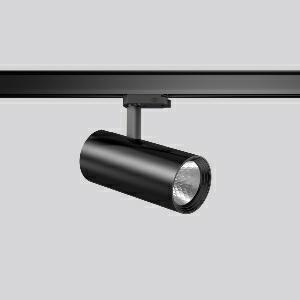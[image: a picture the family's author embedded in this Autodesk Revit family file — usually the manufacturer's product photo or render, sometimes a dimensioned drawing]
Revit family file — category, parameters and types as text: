
# Revit family: deecos_s_mini_742196_003_b451
name_source: partatom
category: Lighting Fixtures
units: mm (PartAtom-declared; Revit-internal decimal feet)

## family parameters
Cut with Voids When Loaded = No
Host = Face
Light Source = No
Part Type = Normal
Room Calculation Point = No
Round Connector Dimension = Use Diameter
Shared = No

## types (1)
- DEECOS S mini (1 x LED Modul 930, 2450 lm, 3000)
    Apparent Load = 20 VA
    Approval mark = CE
    CIE Flux Codes = 99 100 100 100 100
    Color Rendering = 90
    Color Temperature = 3000
    Default Elevation = 1800 mm
    Description = Series: DEECOS S mini
LED surface-mounted projector in modern design with no visible cooling ribs. Housing: die-cast aluminium, powder-coated. Rotation range: 356°. Swivel range: 90°. Black plastic ring and recessed LED to prevent glare from the side. Optical assembly with reflector made of MIRO-Silver with 98% total light reflection for outstanding efficiency - can be changed without tools. Best colour rendering index Ra>90. With multi adaptor for 3-circuit tracks 230 V. Suitable for Track on ceiling, Wall track. High quality converter without flickering and stroboscopic effect. The following accessories can be mounted without use of tools: interchangeable lenses, decorative glasses, honeycomb louvre, clear and frosted diffusers, white interchangeable plastic ring. 
Colour: deep black, matt (RAL 9005)
Diameter: 87 mm
Height: 214 mm
Lamp: LED
Socket: without socket
Colour temperature: 3000K
Colour rendering index (CRI): 92
System power: 20 W
Rated luminous flux: 2450 lm
Luminous efficiency: 123 lm/W
Control gear: Regulated power supply
Protection class: I
Type of protection: IP 20
    Height = 214 mm
    Lamp = 1 x LED Modul 930
    Lamp Light Flux = 2450 lm
    Lamp count = 1
    Length = 87 mm
    Lifetime = 50000 h
    Luminous efficacy = 123 lm/W
    Manufacturer = RZB
    ModVariant = No
    Model = 742196.003
    Mounting Place = Ceiling
    Mounting Type = Rail mounted
    Number of Poles = 1
    OnlyDefault = Yes
    Power Factor = 1
    Product Name = DEECOS S mini
    Product group = Track mounted projectors
    ProductGroupID = 301
    Protection Class = Protection class I
    Protection Degree = IP 20
    RLX_Detail_Level = 1
    RLX_Emergency_Light_Flux = 0 lm
    RLX_Emergency_Type = 0
    RLX_Emergency_Type_DB = No
    RlxData = <blob elided: 38757 chars, md5=056aba45>
    Socket = socket
    Standby Power = 0 W
    System Light Flux = 2450 lm
    System Power = 20 W
    Type Comments = Product without accessories
    Type Image = 741926.003.jpg
    URL = http://relux.com
    VarID = ---
    Voltage = 230 V
    Voltage Range = 220-240 V
    Weight = 0.00 kg
    Width = 0 mm  [stored 0 ft]

note: [stored X ft] marks values corroborated as IEEE doubles in the binary element streams (Revit-internal decimal feet)

## geometry (parser evidence)
native form markers: Blend x4, Sweep x11
no freeform markers — native parametric forms only
